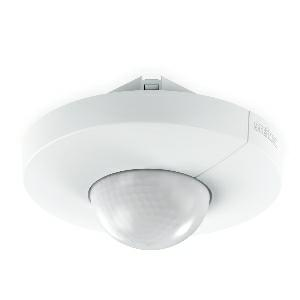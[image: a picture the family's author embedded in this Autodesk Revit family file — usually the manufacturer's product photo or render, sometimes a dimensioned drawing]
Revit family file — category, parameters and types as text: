
# Revit family: is_345_057305
name_source: partatom
category: Elektroinstallationen
revit_build: Autodesk Revit 2016 (Build: 20190508_0715(x64)
units: mm (PartAtom-declared; Revit-internal decimal feet)

## family parameters
Basisbauteil = Fläche
Beim Laden mit Abzugskörper schneiden = Nein
Bemaßung runder Anschluss = Durchmesser verwenden
Beschriftungsausrichtung beibehalten = Nein
Gemeinsam genutzt = Nein
Raumberechnungspunkt = Nein
Teiletyp = Normal

## types (1)
- IS 345
    Apparent Load = 0 VA
    Beschreibung = Type: Motion detectors; Dimensions (Ø x H): 124 x 78 mm; Mains power supply: 12 – 22,5 V / 50 – 60 Hz; Sensor Technology: passive infrared; Application, place: Indoors; Application, room: corridor / aisle, multi-storey / underground car park, Indoors; Installation site: ceiling; Installation: Concealed wiring; Switching zones: 280 switching zones; Electronic scalability: No; Mechanical scalability: No; Mounting height: 2,5 – 5 m; Optimum mounting height: 2,8 m; Detection angle: 360 °; Angle of aperture: 45 °; Sneak-by guard: Yes; Capability of masking out individual segments: Yes; Reach, radial: 12 x 6 m (72 m²); Reach, tangential: 23 x 6 m (138 m²); Twilight setting TEACH: Yes; Twilight setting: 2 – 1000 lx; Time setting: 5 sec – 15 min; Control output, Dali: Addressable/slave; Constant-lighting control: No; Basic light level function: No; Basic light level function time: 1-30 min, all night; With bus coupling: Yes; Settings via: Bus; With remote control: No; Interconnection: Yes; IP-rating: IP20; Material: Plastic; Ambient temperature: -20 – 50 °C; Colour: white; Colour, RAL: 9003; Manufacturer's Warranty: 5 years; Version: DALI-2 IPD - concealed, rd.; PU1, EAN: 4007841057305
    Height = 0 mm  [stored 0 ft]
    Hersteller = Steinel
    Length = 124 mm  [stored 0.406824 ft]
    Maximum range = 11.589 m
    ModVariant = Nein
    Modell = 057305
    Mounting Place = Ceiling
    Mounting Type = Recessed
    Number of Poles = 1
    OnlyDefault = Ja
    Power Factor = 1
    Product Name = IS 345
    Product group = Presence detector
    ProductGroupID = 4
    Protection Class = Protection class
    Protection Degree = IP 20
    RlxData = <blob elided: 156373 chars, md5=da48b0fc>
    Sensor characteristics = Stretched
    Sensor type = Passive (infrared)
    SensorDataFile = <blob elided: 5885 chars, md5=98bccc25>
    Type of entry = Motion
    Typenbild = produkt1_057305.jpg
    Typenkommentare = Product without accessories
    URL = http://relux.com
    VarID = ---
    Voltage = 0 V
    Vorgabe-Ansicht = 1800 mm
    Weight = 0.00 kg
    Width = 0 mm  [stored 0 ft]

note: [stored X ft] marks values corroborated as IEEE doubles in the binary element streams (Revit-internal decimal feet)

## geometry (parser evidence)
native form markers: Blend x4, Sweep x19
no freeform markers — native parametric forms only
